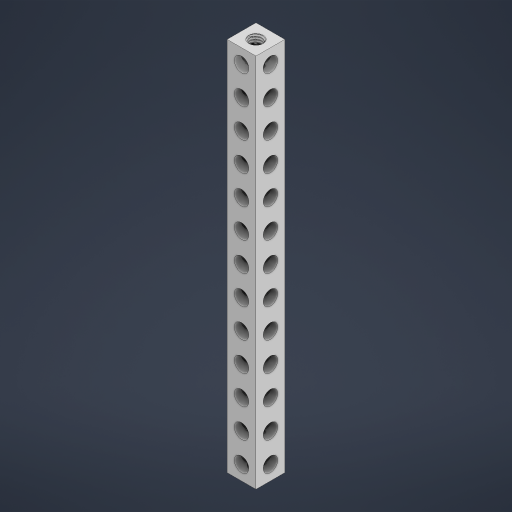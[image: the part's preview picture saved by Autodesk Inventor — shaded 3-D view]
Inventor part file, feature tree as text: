
AUTODESK INVENTOR PART (.ipt)
format: ipt  version: 2023 (Build 270158000, 158)  size: 1,408,000 bytes
history: native  units: in
note: dims shown in document units (in); Inventor stores cm internally (conversion verified against a paired STEP export)
features: mirror x1
ambient origin geometry x8: Origin, YZ Plane, XZ Plane, XY Plane, X Axis, Y Axis, Z Axis, Center Point
bodies: Solid1 (feature_tree)
feature tree (1):
  mirror  "Mirror3"
